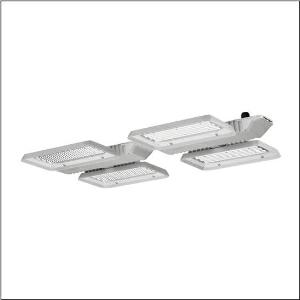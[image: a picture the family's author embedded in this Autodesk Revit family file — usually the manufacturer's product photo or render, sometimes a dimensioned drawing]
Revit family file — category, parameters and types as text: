
# Revit family: highbay_11_51hla1d24mca
name_source: partatom
category: Lighting Fixtures
units: mm (PartAtom-declared; Revit-internal decimal feet)

## family parameters
Cut with Voids When Loaded = No
Host = Face
Light Source = No
Part Type = Normal
Room Calculation Point = No
Round Connector Dimension = Use Diameter
Shared = No

## types (1)
- --- (1 x LED, 28120 lm, 162.4 W, 4000K)
    Apparent Load = 162 VA
    CIE Flux Codes = 88 95 99 100 99
    Color Rendering = 80
    Color Temperature = 4000K
    Default Elevation = 1800 mm
    Description = Highbay 11, LED high bay luminaire, primary light control with lens, of PMMA, light emission: direct distribution, primary light characteristic: symmetric, installation type: suspended mounting, surface-mounted, for 2x 2x LED, rated luminous flux: 28.120lm, luminous efficacy: 173lm/W, light colour: 840, colour temperature: 4000K, control gear: ECG DALI, with terminal, 5-pole, max. 2.5mm², mains connection: 230..240V, AC, 50/60Hz, rated input power: 162W, LED unit, of diecast aluminium, unplated, bead blasted, silver, length: 940mm, width: 500mm, height: 65mm, housing, of diecast aluminium, uncoated, bead blasted, silver, protection rating (complete): IP65, insulation class (complete): insulation class I (protective earthing), certification: CE, ENEC, VDE, UKCA, protection symbol: D, impact resistance: IK08 with glass or PC cover, permissible operating ambient temperature: -35..+55°C, reducing of maximum allowable ambient temperature of 5°C with ceiling mounting, corresponds to IFS (International Featured Standards) requirements for safety and quality in the food industry, packaging unit: 1 piece
    Height = 95 mm
    Lamp = 1 x LED
    Lamp Light Flux = 28120 lm
    Lamp Power = 162.4 W
    Lamp count = 1
    Length = 939 mm
    Luminous efficacy = 173 lm/W
    Manufacturer = Siteco
    ModVariant = No
    Model = 51HLA1D24MCA
    Mounting Place = Ceiling
    Mounting Type = Pendant
    Number of Poles = 1
    OnlyDefault = Yes
    Power Factor = 1
    Product Name = Highbay 11
    Product group = LED high bay luminaire
    ProductGroupID = 903
    Protection Class = Protection class I
    Protection Degree = IP 65
    RLX_Detail_Level = 1
    RLX_Emergency_Light_Flux = 0 lm
    RLX_Emergency_Type = 0
    RLX_Emergency_Type_DB = No
    RlxData = <blob elided: 100489 chars, md5=05683eb5>
    Socket = socket
    Standby Power = 0 W
    System Light Flux = 28120 lm
    System Power = 162 W
    Type Comments = factory setting: luminous flux: 100 % | dim-lin: 254 | 460 mA
    Type Image = l_1003428.jpg
    URL = http://relux.com
    VarID = @adj_146193
    Voltage = 0 V
    Weight = 0.00 kg
    Width = 501 mm

## geometry (parser evidence)
native form markers: Blend x4, Sweep x12
no freeform markers — native parametric forms only
